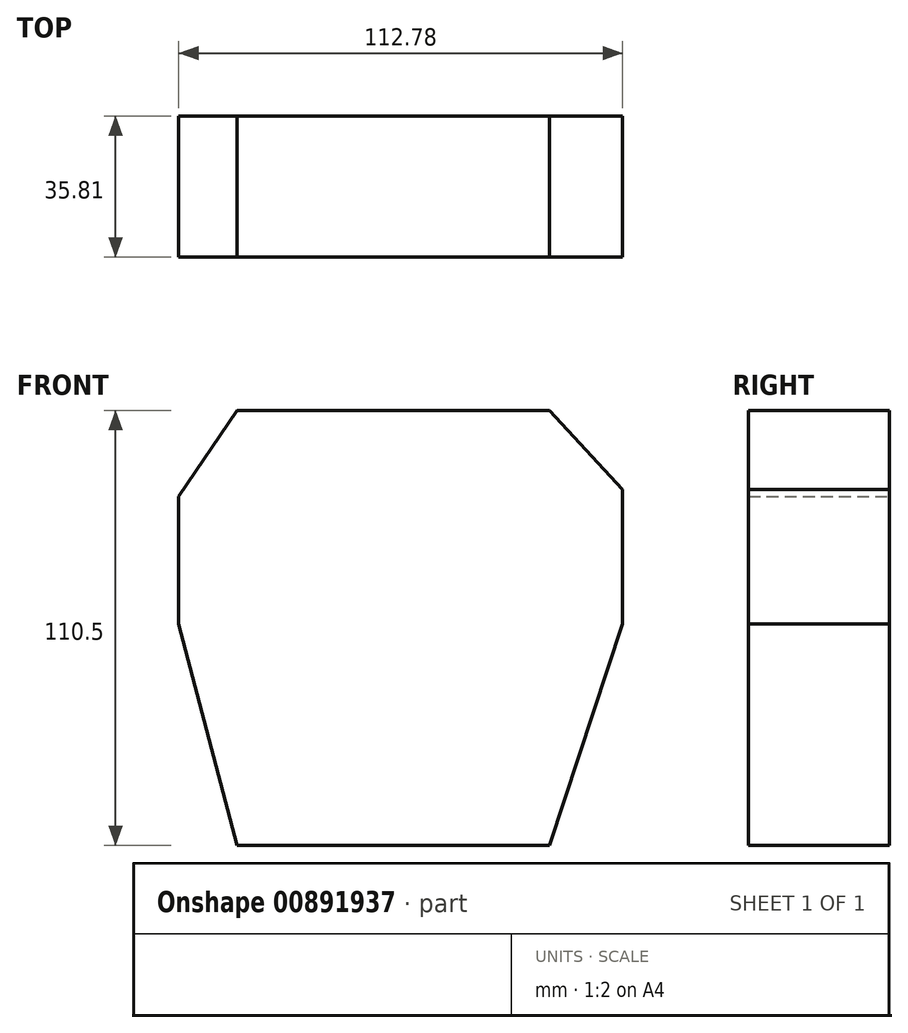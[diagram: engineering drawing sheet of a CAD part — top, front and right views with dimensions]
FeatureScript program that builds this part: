
annotation { "Feature Type Name" : "Feature", "Feature Type Description" : "" }
export const myFeature = defineFeature(function(context is Context, id is Id, definition is map)
    precondition{}
    {
        {
            var Q0;
            Q0=qCreatedBy(makeId("Front.planeOp"),FACE);
            var sketch = newSketch(context, id + "F0", { "sketchPlane" : qUnion([Q0])});
            skLineSegment(sketch, "E0", {"start": v(-54.49, 33.4) * mm, "end": v(-39.69, 55.25) * mm});
            skLineSegment(sketch, "E1", {"start": v(-39.69, 55.25) * mm, "end": v(39.69, 55.25) * mm});
            skLineSegment(sketch, "E2", {"start": v(39.69, 55.25) * mm, "end": v(58.29, 35.16) * mm});
            skLineSegment(sketch, "E3", {"start": v(58.29, 35.16) * mm, "end": v(58.29, 0.97) * mm});
            skLineSegment(sketch, "E4", {"start": v(58.29, 0.97) * mm, "end": v(39.69, -55.25) * mm});
            skLineSegment(sketch, "E5", {"start": v(39.69, -55.25) * mm, "end": v(-39.69, -55.25) * mm});
            skLineSegment(sketch, "E6", {"start": v(-39.69, -55.25) * mm, "end": v(-54.49, 0.97) * mm});
            skLineSegment(sketch, "E7", {"start": v(-54.49, 0.97) * mm, "end": v(-54.49, 33.4) * mm});
            skLineSegment(sketch, "E8", {"start": v(0, 55.25) * mm, "end": v(0, -55.25) * mm, "construction": true});
            skSolve(sketch);
        }
        {
            var Q0;
            Q0 = qSketchRegion(id + "F0", true);
            extrude(context, id + "F1", {"entities" : qUnion([Q0]), "depth" : 35.81 * mm, "offsetDistance" : 25.4 * mm});
        }
    });
